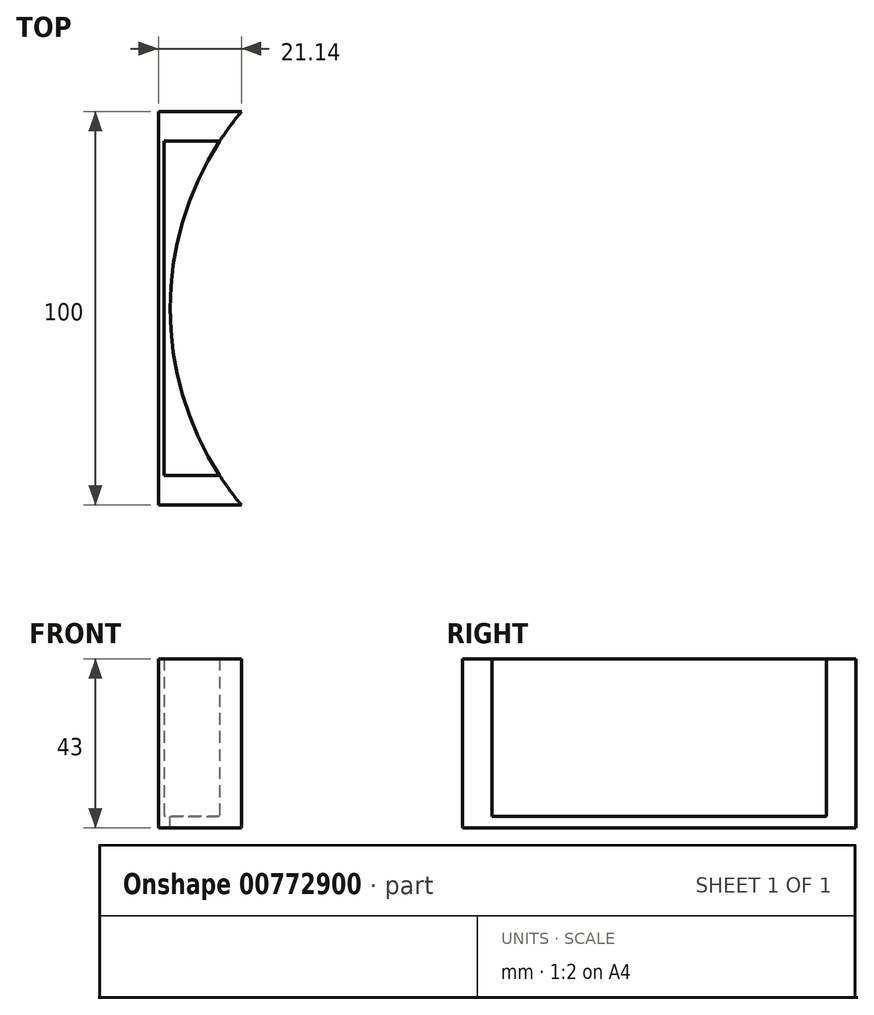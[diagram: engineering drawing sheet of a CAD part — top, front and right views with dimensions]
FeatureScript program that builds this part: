
annotation { "Feature Type Name" : "Feature", "Feature Type Description" : "" }
export const myFeature = defineFeature(function(context is Context, id is Id, definition is map)
    precondition{}
    {
        {
            var Q0;
            Q0=qCreatedBy(makeId("Top.planeOp"),FACE);
            var sketch = newSketch(context, id + "F0", { "sketchPlane" : qUnion([Q0])});
            skLineSegment(sketch, "E0", {"start": v(-145.02, 50.46) * mm, "end": v(-126.9, 50.46) * mm});
            skLineSegment(sketch, "E1", {"start": v(-145.01, -49.54) * mm, "end": v(-126.88, -49.54) * mm});
            skArc(sketch, "E2", {"start": v(-126.9, 50.46) * mm, "mid": v(-145, 0.45) * mm, "end": v(-126.88, -49.54) * mm});
            skLineSegment(sketch, "E3", {"start": v(-145.01, -42.04) * mm, "end": v(-132.42, -42.04) * mm});
            skLineSegment(sketch, "E4", {"start": v(-145.02, 42.96) * mm, "end": v(-132.43, 42.96) * mm});
            skLineSegment(sketch, "E5", {"start": v(-145.02, 50.46) * mm, "end": v(-148.02, 50.46) * mm});
            skLineSegment(sketch, "E6", {"start": v(-148.02, 50.46) * mm, "end": v(-148.02, -49.54) * mm});
            skLineSegment(sketch, "E7", {"start": v(-148.02, -49.54) * mm, "end": v(-145.01, -49.54) * mm});
            skArc(sketch, "E8", {"start": v(-126.9, 50.46) * mm, "mid": v(-145.02, 0.45) * mm, "end": v(-126.88, -49.54) * mm});
            skLineSegment(sketch, "E9", {"start": v(-148.02, 50.46) * mm, "end": v(-146.52, 50.46) * mm});
            skLineSegment(sketch, "E10", {"start": v(-146.52, 50.46) * mm, "end": v(-146.52, -49.54) * mm});
            skLineSegment(sketch, "E11", {"start": v(-132.42, -42.04) * mm, "end": v(-146.52, -42.04) * mm});
            skLineSegment(sketch, "E12", {"start": v(-132.43, 42.96) * mm, "end": v(-146.52, 42.96) * mm});
            skSolve(sketch);
        }
        {
            var Q0;
            {var subQ4=sQuery(id+"F0.wireOp",EDGE,"E0");Q0=makeQuery(id+"F0.imprint","IMPRINT",FACE,{"disambiguationData":[TD([[makeQuery(id+"F0.imprint","IMPRINT",EDGE,{"derivedFrom":subQ4}),-1.0]])]});}
            var Q1;
            {var subQ4=sQuery(id+"F0.wireOp",EDGE,"E6");Q1=makeQuery(id+"F0.imprint","IMPRINT",FACE,{"disambiguationData":[TD([[makeQuery(id+"F0.imprint","IMPRINT",EDGE,{"derivedFrom":subQ4}),1.0]])]});}
            var Q2;
            {var subQ6=sQuery(id+"F0.wireOp",EDGE,"E1");Q2=makeQuery(id+"F0.imprint","IMPRINT",FACE,{"disambiguationData":[TD([[makeQuery(id+"F0.imprint","IMPRINT",EDGE,{"derivedFrom":subQ6}),1.0]])]});}
            var Q3;
            {var subQ0=sQuery(id+"F0.wireOp",EDGE,"E11");var subQ3=makeQuery(id+"F0.imprint","IMPRINT",VERTEX,{"derivedFrom":subQ0});Q3=makeQuery(id+"F0.imprint","IMPRINT",FACE,{"disambiguationData":[TD([[makeQuery(id+"F0.imprint","IMPRINT",EDGE,{"disambiguationData":[TD([[subQ3,1.0]])],"derivedFrom":subQ0}),-1.0]])]});}
            extrude(context, id + "F1", {"entities" : qUnion([Q0, Q1, Q2, Q3]), "oppositeDirection" : true, "depth" : 3 * mm, "offsetDistance" : 25 * mm});
        }
        {
            var Q0;
            {var subQ4=sQuery(id+"F0.wireOp",EDGE,"E0");Q0=makeQuery(id+"F0.imprint","IMPRINT",FACE,{"disambiguationData":[TD([[makeQuery(id+"F0.imprint","IMPRINT",EDGE,{"derivedFrom":subQ4}),-1.0]])]});}
            var Q1;
            {var subQ6=sQuery(id+"F0.wireOp",EDGE,"E1");Q1=makeQuery(id+"F0.imprint","IMPRINT",FACE,{"disambiguationData":[TD([[makeQuery(id+"F0.imprint","IMPRINT",EDGE,{"derivedFrom":subQ6}),1.0]])]});}
            var Q2;
            {var subQ4=sQuery(id+"F0.wireOp",EDGE,"E6");Q2=makeQuery(id+"F0.imprint","IMPRINT",FACE,{"disambiguationData":[TD([[makeQuery(id+"F0.imprint","IMPRINT",EDGE,{"derivedFrom":subQ4}),1.0]])]});}
            extrude(context, id + "F2", {"entities" : qUnion([Q0, Q1, Q2]), "operationType" : NewBodyOperationType.ADD, "depth" : 40 * mm, "offsetDistance" : 25 * mm});
        }
    });
